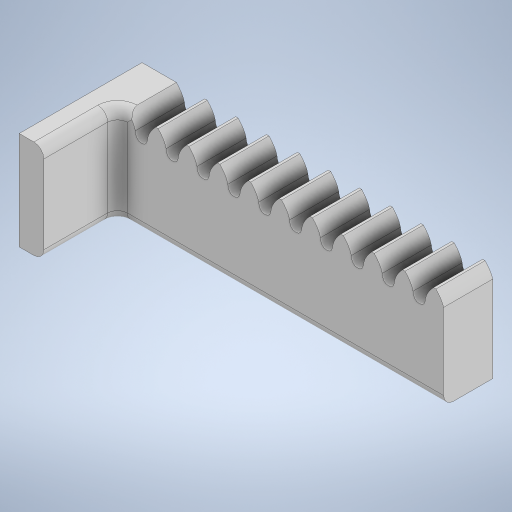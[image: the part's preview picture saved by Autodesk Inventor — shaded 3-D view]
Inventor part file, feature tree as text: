
AUTODESK INVENTOR PART (.ipt)
format: ipt  version: 2023 (Build 270158000, 158)  size: 370,688 bytes
history: native  units: mm
features: sketch x3, extrude x3, fillet x2, pattern_linear x1
ambient origin geometry x8: Origin, YZ Plane, XZ Plane, XY Plane, X Axis, Y Axis, Z Axis, Center Point
bodies: Body1 (feature_tree)
feature tree (9):
  sketch  "Sketch1"  dims[d17=66.4mm d18=20.0mm]
  extrude  "Extrusion3"  Depth=20.0mm
  extrude  "Extrusion4"  Depth=10.0mm TaperAngle=0.0deg
  pattern_linear  "Rectangular Pattern1"  Count1=15 Spacing1=6.283185mm
  extrude  "Extrusion5"  Depth=2.0mm
  fillet  "Fillet1"  Radius=20.0mm
  fillet  "Fillet2"  Radius=5.0mm
  sketch  "Sketch3"  dims[d19=2.0mm d20=10.0mm d21=0.0mm]
  sketch  "Sketch4"  dims[d22=10.0mm d23=0.0mm d24=150.0mm d26=6.283185mm d27=25.0mm d28=20.0mm d29=5.0mm d30=0.0mm d31=2.0mm d32=2.0mm]
